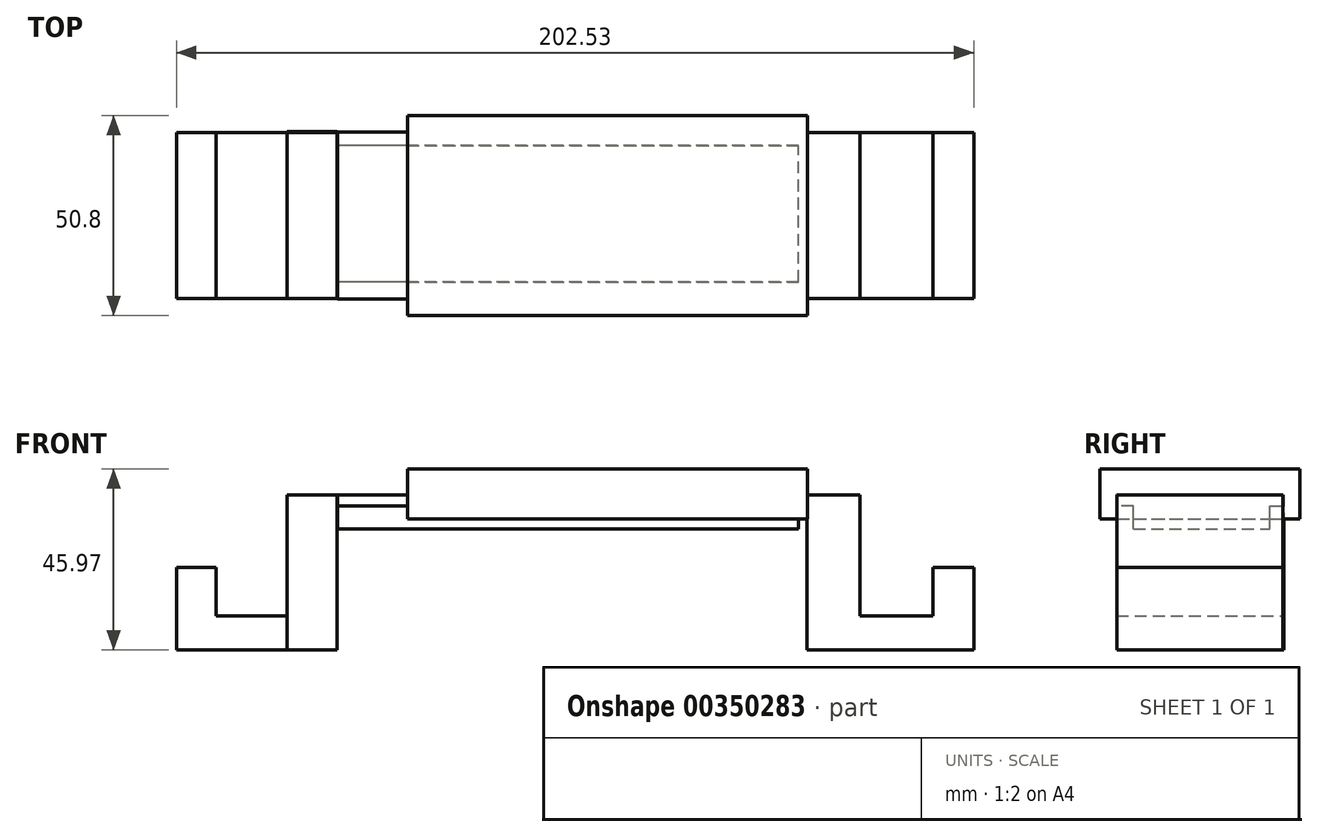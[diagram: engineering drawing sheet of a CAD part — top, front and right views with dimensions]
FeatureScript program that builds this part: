
annotation { "Feature Type Name" : "Feature", "Feature Type Description" : "" }
export const myFeature = defineFeature(function(context is Context, id is Id, definition is map)
    precondition{}
    {
        {
            var Q0;
            Q0=qCreatedBy(makeId("Top.planeOp"),FACE);
            var sketch = newSketch(context, id + "F0", { "sketchPlane" : qUnion([Q0])});
            skLineSegment(sketch, "E0.bottom", {"start": v(0, 0) * mm, "end": v(50.8, 0) * mm});
            skLineSegment(sketch, "E0.top", {"start": v(0, 25.4) * mm, "end": v(50.8, 25.4) * mm});
            skLineSegment(sketch, "E0.left", {"start": v(0, 0) * mm, "end": v(0, 25.4) * mm});
            skLineSegment(sketch, "E0.right", {"start": v(50.8, 0) * mm, "end": v(50.8, 25.4) * mm});
            skLineSegment(sketch, "E1.MirrorCS", {"start": v(0, -25.4) * mm, "end": v(50.8, -25.4) * mm});
            skLineSegment(sketch, "E2.MirrorCS", {"start": v(0, 0) * mm, "end": v(0, -25.4) * mm});
            skLineSegment(sketch, "E3.MirrorCS", {"start": v(50.8, 0) * mm, "end": v(50.8, -25.4) * mm});
            skLineSegment(sketch, "E4.MirrorCS", {"start": v(0, 25.4) * mm, "end": v(-50.8, 25.4) * mm});
            skLineSegment(sketch, "E5.MirrorCS", {"start": v(-50.8, 0) * mm, "end": v(-50.8, 25.4) * mm});
            skLineSegment(sketch, "E6.MirrorCS", {"start": v(0, 0) * mm, "end": v(-50.8, 0) * mm});
            skLineSegment(sketch, "E7.MirrorCS", {"start": v(0, -25.4) * mm, "end": v(-50.8, -25.4) * mm});
            skLineSegment(sketch, "E8.MirrorCS", {"start": v(-50.8, 0) * mm, "end": v(-50.8, -25.4) * mm});
            skSolve(sketch);
        }
        {
            var Q0;
            Q0 = qSketchRegion(id + "F0", true);
            extrude(context, id + "F1", {"entities" : qUnion([Q0]), "depth" : 12.7 * mm});
        }
        {
            var Q0;
            Q0=qCreatedBy(makeId("Right.planeOp"),FACE);
            var sketch = newSketch(context, id + "F2", { "sketchPlane" : qUnion([Q0])});
            skLineSegment(sketch, "E9.bottom", {"start": v(-16.84, -2.49) * mm, "end": v(17.8, -2.49) * mm});
            skLineSegment(sketch, "E9.top", {"start": v(-16.84, 6.13) * mm, "end": v(17.8, 6.13) * mm});
            skLineSegment(sketch, "E9.left", {"start": v(-16.84, -2.49) * mm, "end": v(-16.84, 6.13) * mm});
            skLineSegment(sketch, "E9.right", {"start": v(17.8, -2.49) * mm, "end": v(17.8, 6.13) * mm});
            skLineSegment(sketch, "E10.bottom", {"start": v(-16.84, 6.13) * mm, "end": v(-21.25, 6.13) * mm});
            skLineSegment(sketch, "E10.top", {"start": v(-16.84, 3.25) * mm, "end": v(-21.25, 3.25) * mm});
            skLineSegment(sketch, "E10.left", {"start": v(-16.84, 6.13) * mm, "end": v(-16.84, 3.25) * mm});
            skLineSegment(sketch, "E10.right", {"start": v(-21.25, 6.13) * mm, "end": v(-21.25, 3.25) * mm});
            skLineSegment(sketch, "E11.MirrorCS", {"start": v(16.84, 3.25) * mm, "end": v(21.25, 3.25) * mm});
            skLineSegment(sketch, "E12.MirrorCS", {"start": v(16.84, 6.13) * mm, "end": v(21.25, 6.13) * mm});
            skLineSegment(sketch, "E13", {"start": v(21.25, 6.13) * mm, "end": v(21.25, 3.25) * mm});
            skLineSegment(sketch, "E14", {"start": v(16.84, 6.13) * mm, "end": v(16.84, 3.25) * mm});
            skSolve(sketch);
        }
        {
            var Q0;
            Q0 = qSketchRegion(id + "F2", true);
            extrude(context, id + "F3", {"entities" : qUnion([Q0]), "operationType" : NewBodyOperationType.ADD, "depth" : 48.5 * mm, "hasSecondDirection" : true, "secondDirectionOppositeDirection" : true, "secondDirectionDepth" : 68.58 * mm});
        }
        {
            var Q0;
            Q0=qCreatedBy(makeId("Front.planeOp"),FACE);
            var sketch = newSketch(context, id + "F4", { "sketchPlane" : qUnion([Q0])});
            skLineSegment(sketch, "E15.bottom", {"start": v(-68.66, 6.15) * mm, "end": v(-81.36, 6.15) * mm});
            skLineSegment(sketch, "E15.top", {"start": v(-68.66, -33.27) * mm, "end": v(-81.36, -33.27) * mm});
            skLineSegment(sketch, "E15.left", {"start": v(-68.66, 6.15) * mm, "end": v(-68.66, -33.27) * mm});
            skLineSegment(sketch, "E15.right", {"start": v(-81.36, 6.15) * mm, "end": v(-81.36, -33.27) * mm});
            skLineSegment(sketch, "E16.bottom", {"start": v(-81.36, -24.62) * mm, "end": v(-99.44, -24.62) * mm});
            skLineSegment(sketch, "E16.top", {"start": v(-81.36, -33.27) * mm, "end": v(-99.44, -33.27) * mm});
            skLineSegment(sketch, "E16.left", {"start": v(-81.36, -24.62) * mm, "end": v(-81.36, -33.27) * mm});
            skLineSegment(sketch, "E16.right", {"start": v(-99.44, -24.62) * mm, "end": v(-99.44, -33.27) * mm});
            skLineSegment(sketch, "E17.bottom", {"start": v(-99.44, -33.27) * mm, "end": v(-109.44, -33.27) * mm});
            skLineSegment(sketch, "E17.top", {"start": v(-99.44, -12.3) * mm, "end": v(-109.44, -12.3) * mm});
            skLineSegment(sketch, "E17.left", {"start": v(-99.44, -33.27) * mm, "end": v(-99.44, -12.3) * mm});
            skLineSegment(sketch, "E17.right", {"start": v(-109.44, -33.27) * mm, "end": v(-109.44, -12.3) * mm});
            skLineSegment(sketch, "E18.bottom", {"start": v(50.78, 6.15) * mm, "end": v(64.24, 6.15) * mm});
            skLineSegment(sketch, "E18.top", {"start": v(50.78, -33.27) * mm, "end": v(64.24, -33.27) * mm});
            skLineSegment(sketch, "E18.left", {"start": v(50.78, 6.15) * mm, "end": v(50.78, -33.27) * mm});
            skLineSegment(sketch, "E18.right", {"start": v(64.24, 6.15) * mm, "end": v(64.24, -33.27) * mm});
            skLineSegment(sketch, "E19.bottom", {"start": v(64.24, -33.27) * mm, "end": v(82.7, -33.27) * mm});
            skLineSegment(sketch, "E19.top", {"start": v(64.24, -24.62) * mm, "end": v(82.7, -24.62) * mm});
            skLineSegment(sketch, "E19.left", {"start": v(64.24, -33.27) * mm, "end": v(64.24, -24.62) * mm});
            skLineSegment(sketch, "E19.right", {"start": v(82.7, -33.27) * mm, "end": v(82.7, -24.62) * mm});
            skLineSegment(sketch, "E20.bottom", {"start": v(82.7, -33.27) * mm, "end": v(93.09, -33.27) * mm});
            skLineSegment(sketch, "E20.top", {"start": v(82.7, -12.3) * mm, "end": v(93.09, -12.3) * mm});
            skLineSegment(sketch, "E20.left", {"start": v(82.7, -33.27) * mm, "end": v(82.7, -12.3) * mm});
            skLineSegment(sketch, "E20.right", {"start": v(93.09, -33.27) * mm, "end": v(93.09, -12.3) * mm});
            skSolve(sketch);
        }
        {
            var Q0;
            Q0=makeQuery(id+"F4.imprint","IMPRINT",FACE,{"disambiguationData":[TD([[makeQuery(id+"F4.imprint","IMPRINT",EDGE,{"derivedFrom":sQuery(id+"F4.wireOp",EDGE,"E15.bottom")}),1.0]])]});
            extrude(context, id + "F5", {"entities" : qUnion([Q0]), "depth" : 21.08 * mm, "hasSecondDirection" : true, "secondDirectionOppositeDirection" : true, "secondDirectionDepth" : 21.34 * mm});
        }
        {
            var Q0;
            Q0 = qSketchRegion(id + "F4", true);
            extrude(context, id + "F6", {"entities" : qUnion([Q0]), "depth" : 21.08 * mm, "hasSecondDirection" : true, "secondDirectionOppositeDirection" : true, "secondDirectionDepth" : 21.08 * mm});
        }
    });
